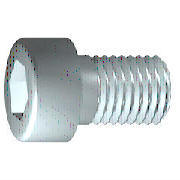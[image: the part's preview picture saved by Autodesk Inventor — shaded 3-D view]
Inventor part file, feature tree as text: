
AUTODESK INVENTOR PART (.ipt)
format: ipt  version: 2017 (Build 210142000, 142)  size: 188,928 bytes
history: native  units: mm (DEFAULTED — no unit token found)
features: sketch x2, extrude x1, plane x1, fillet x1
ambient origin geometry x7: Origin, YZ Plane, XY Plane, X Axis, Y Axis, Z Axis, Center Point
bodies: Solid1 (feature_tree), Body (feature_tree)
feature tree (5):
  extrude  "Slot"  Depth=3.0mm
  plane  "Work Plane1"
  fillet  "Fillet2"  Radius=3.0mm
  sketch  "Sketch1"  dims[d1=10.693275mm d2=0.306825mm d3=3.0mm]
  sketch  "Sketch2"  dims[d4=1.5mm d5=60.0deg d6=3.0mm d7=3.0mm d8=2.886751mm d9=5.5mm d10=90.0deg d11=10.0mm d12=0.0mm d13=10.693275mm d14=0.0mm d15=0.306725mm d16=0.306725mm d17=0.3mm d19=0.0mm d26=12.0mm d27=45.0deg d28=0.0mm d29=0.0mm d30=0.1mm]
